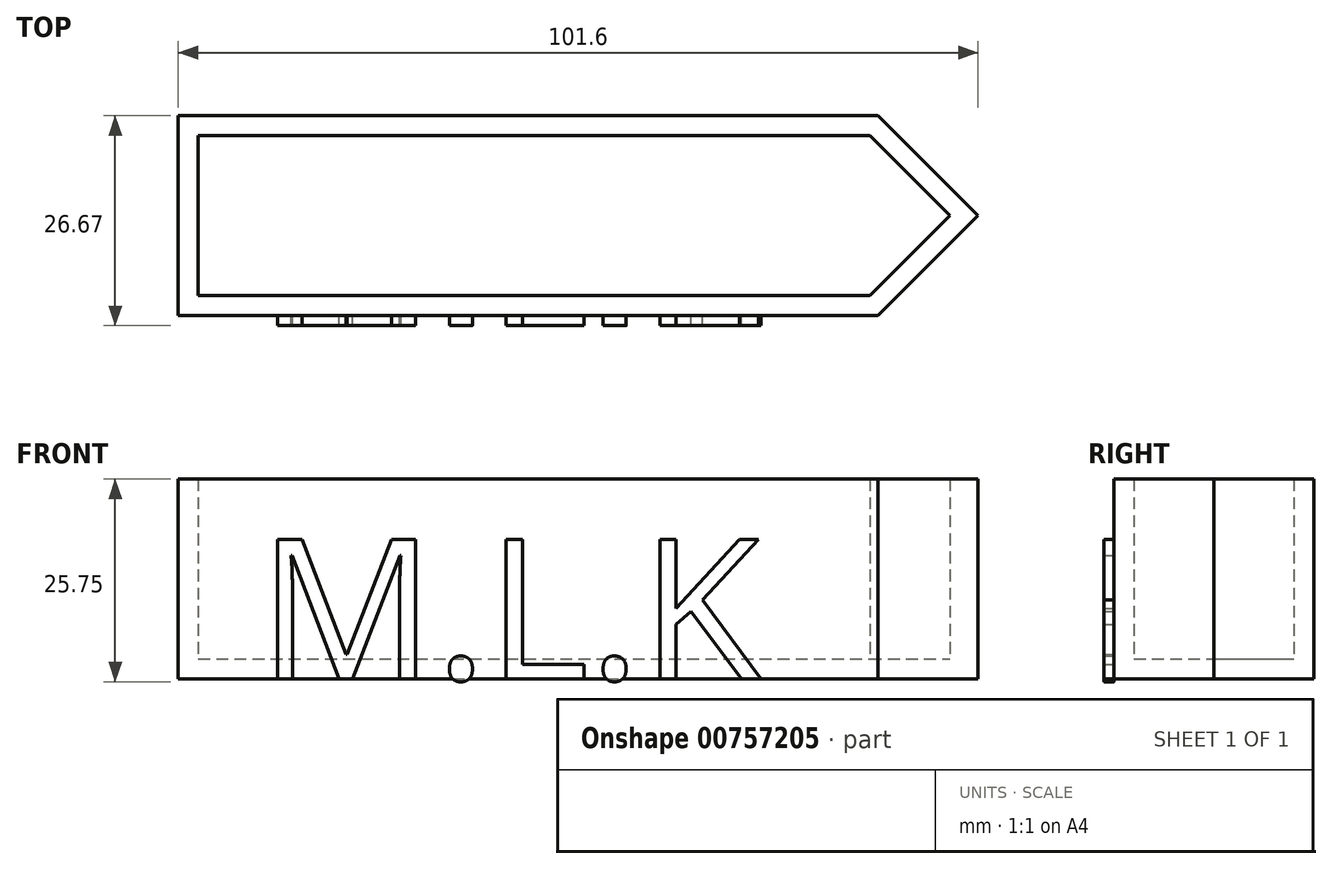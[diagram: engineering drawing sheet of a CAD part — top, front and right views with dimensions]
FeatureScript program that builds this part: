
annotation { "Feature Type Name" : "Feature", "Feature Type Description" : "" }
export const myFeature = defineFeature(function(context is Context, id is Id, definition is map)
    precondition{}
    {
        {
            var Q0;
            Q0=qCreatedBy(makeId("Top.planeOp"),FACE);
            var sketch = newSketch(context, id + "F0", { "sketchPlane" : qUnion([Q0])});
            skLineSegment(sketch, "E0", {"start": v(-50.96, 5.99) * mm, "end": v(-50.96, 31.39) * mm});
            skLineSegment(sketch, "E1", {"start": v(-50.96, 31.39) * mm, "end": v(37.94, 31.39) * mm});
            skLineSegment(sketch, "E2", {"start": v(-50.96, 5.99) * mm, "end": v(37.94, 5.99) * mm});
            skLineSegment(sketch, "E3", {"start": v(-50.96, 18.69) * mm, "end": v(50.64, 18.69) * mm});
            skLineSegment(sketch, "E4", {"start": v(50.64, 18.69) * mm, "end": v(37.94, 31.39) * mm});
            skLineSegment(sketch, "E5", {"start": v(37.94, 5.99) * mm, "end": v(50.64, 18.69) * mm});
            skSolve(sketch);
        }
        {
            var Q0;
            {var subQ0=sQuery(id+"F0.wireOp",EDGE,"E1");Q0=makeQuery(id+"F0.imprint","IMPRINT",FACE,{"disambiguationData":[TD([[makeQuery(id+"F0.imprint","IMPRINT",EDGE,{"derivedFrom":subQ0}),-1.0]])]});}
            var Q1;
            {var subQ0=sQuery(id+"F0.wireOp",EDGE,"E2");Q1=makeQuery(id+"F0.imprint","IMPRINT",FACE,{"disambiguationData":[TD([[makeQuery(id+"F0.imprint","IMPRINT",EDGE,{"derivedFrom":subQ0}),1.0]])]});}
            extrude(context, id + "F1", {"entities" : qUnion([Q0, Q1]), "depth" : 25.4 * mm, "offsetDistance" : 25.4 * mm});
        }
        {
            var Q0;
            Q0=makeQuery(id+"F1.opExtrude","CAP_FACE",FACE,{"disambiguationData":[OSD([sQuery(id+"F0.wireOp",EDGE,"E0"),sQuery(id+"F0.wireOp",EDGE,"E1"),sQuery(id+"F0.wireOp",EDGE,"E2"),sQuery(id+"F0.wireOp",EDGE,"E4"),sQuery(id+"F0.wireOp",EDGE,"E5")])],"isStart":false});
            shell(context, id + "F2", {"entities" : qUnion([Q0]), "thickness" : 2.54 * mm});
        }
        {
            var Q0;
            Q0=makeQuery(id+"F1.opExtrude","SWEPT_FACE",FACE,{"disambiguationData":[OSD([sQuery(id+"F0.wireOp",EDGE,"E2")])]});
            var sketch = newSketch(context, id + "F3", { "sketchPlane" : qUnion([Q0])});
            skSolve(sketch);
        }
        {
            var Q0;
            {var subQ0=sQuery(id+"F0.wireOp",EDGE,"E2");Q0=makeQuery(id+"F3.imprint","IMPRINT",FACE,{"disambiguationData":[TD([[makeQuery(id+"F3.imprint","IMPRINT",EDGE,{"derivedFrom":makeQuery(id+"F1.opExtrude","CAP_EDGE",EDGE,{"disambiguationData":[OSD([subQ0])],"isStart":true})}),1.0]])]});}
            var sketch = newSketch(context, id + "F4", { "sketchPlane" : qUnion([Q0])});
            skText(sketch, "E6", { "text": "M.L.K", "fontName": "OpenSans-Regular.ttf"});
            const initialGuessF4  = {"E6": [-0.0408, 0, 1, 0, 0.0179]};
            skSetInitialGuess(sketch, initialGuessF4);
            skSolve(sketch);
        }
        {
            var Q0;
            Q0 = qSketchRegion(id + "F4", true);
            extrude(context, id + "F5", {"entities" : qUnion([Q0]), "operationType" : NewBodyOperationType.ADD, "depth" : 1.27 * mm, "offsetDistance" : 25.4 * mm});
        }
    });
